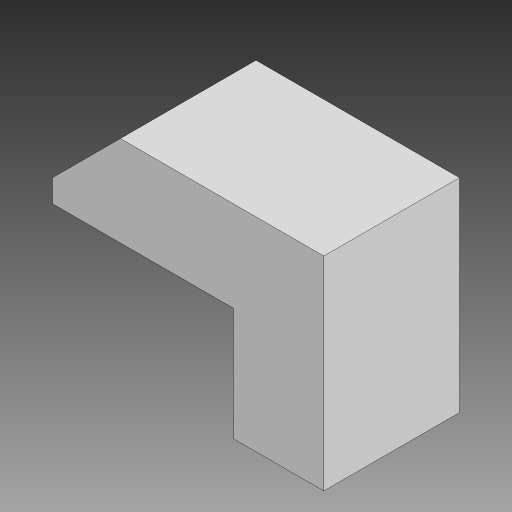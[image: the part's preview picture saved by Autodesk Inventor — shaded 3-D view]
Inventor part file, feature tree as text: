
AUTODESK INVENTOR PART (.ipt)
format: ipt  version: 2023 (Build 270158000, 158)  size: 254,464 bytes
history: native  units: mm
features: other x1, extrude x1, chamfer x1, sketch x1
ambient origin geometry x8: Origin, YZ Plane, XZ Plane, XY Plane, X Axis, Y Axis, Z Axis, Center Point
bodies: Body1 (feature_tree)
feature tree (4):
  other  "Těleso1"
  extrude  "Vysunutí1"  Depth=6.0mm
  chamfer  "Zkosení1"  Distance=2.0mm
  sketch  "Náčrt1"
